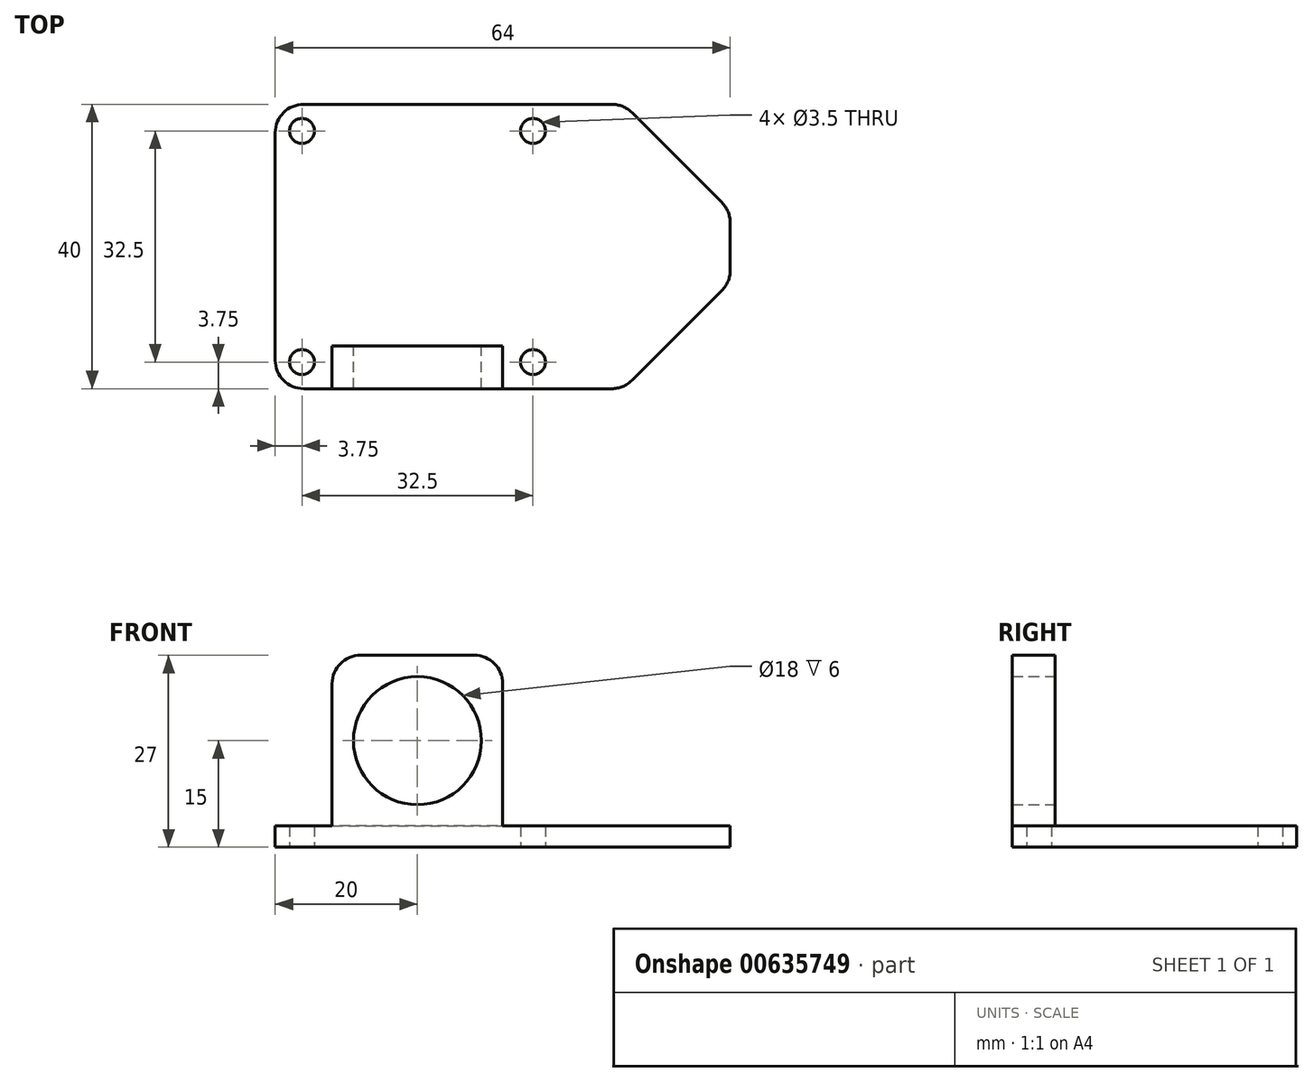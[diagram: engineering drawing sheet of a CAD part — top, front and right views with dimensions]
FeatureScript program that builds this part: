
annotation { "Feature Type Name" : "Feature", "Feature Type Description" : "" }
export const myFeature = defineFeature(function(context is Context, id is Id, definition is map)
    precondition{}
    {
        {
            var Q0;
            Q0=qCreatedBy(makeId("Top.planeOp"),FACE);
            var sketch = newSketch(context, id + "F0", { "sketchPlane" : qUnion([Q0])});
            skLineSegment(sketch, "E0.bottom", {"start": v(20, -20) * mm, "end": v(-20, -20) * mm});
            skLineSegment(sketch, "E0.top", {"start": v(20, 20) * mm, "end": v(-20, 20) * mm});
            skLineSegment(sketch, "E0.left", {"start": v(20, -20) * mm, "end": v(20, 20) * mm});
            skLineSegment(sketch, "E0.right", {"start": v(-20, -20) * mm, "end": v(-20, 20) * mm});
            skPoint(sketch, "E0.middle", {"position": v(0, 0) * mm});
            skCircle(sketch, "E1", {"center": v(-16.25, 16.25) * mm, "radius": 1.75 * mm});
            skCircle(sketch, "E2", {"center": v(16.25, 16.25) * mm, "radius": 1.75 * mm});
            skCircle(sketch, "E3", {"center": v(16.25, -16.25) * mm, "radius": 1.75 * mm});
            skCircle(sketch, "E4", {"center": v(-16.25, -16.25) * mm, "radius": 1.75 * mm});
            skSolve(sketch);
        }
        {
            var Q0;
            Q0=makeQuery(id+"F0.imprint","IMPRINT",FACE,{"disambiguationData":[TD([[makeQuery(id+"F0.imprint","IMPRINT",EDGE,{"derivedFrom":sQuery(id+"F0.wireOp",EDGE,"E0.bottom")}),-1.0]])]});
            extrude(context, id + "F1", {"entities" : qUnion([Q0]), "depth" : 3 * mm, "offsetDistance" : 25 * mm});
        }
        {
            var Q0;
            {var subQ0=sQuery(id+"F0.wireOp",EDGE,"E0.right");Q0=makeQuery(id+"F8QHIOm5U3Bt2tr_1.boolean.opBoolean","MERGE",FACE,{"derivedFrom":[makeQuery(id+"F1.opExtrude","CAP_FACE",FACE,{"disambiguationData":[OSD([sQuery(id+"F0.wireOp",EDGE,"E0.bottom"),sQuery(id+"F0.wireOp",EDGE,"E0.top"),sQuery(id+"F0.wireOp",EDGE,"E0.left"),subQ0,sQuery(id+"F0.wireOp",EDGE,"E1"),sQuery(id+"F0.wireOp",EDGE,"E2"),sQuery(id+"F0.wireOp",EDGE,"E3"),sQuery(id+"F0.wireOp",EDGE,"E4")])],"isStart":false}),makeQuery(id+"F8QHIOm5U3Bt2tr_1.opExtrude","SWEPT_FACE",FACE,{"disambiguationData":[OSD([subQ0]),TDD([makeQuery(id+"F1.opExtrude","CAP_EDGE",EDGE,{"disambiguationData":[OSD([subQ0])],"isStart":false})])]})]});}
            var sketch = newSketch(context, id + "F2", { "sketchPlane" : qUnion([Q0])});
            skLineSegment(sketch, "E5.bottom", {"start": v(-12, -20) * mm, "end": v(12, -20) * mm});
            skLineSegment(sketch, "E5.top", {"start": v(-12, -14) * mm, "end": v(12, -14) * mm});
            skLineSegment(sketch, "E5.left", {"start": v(-12, -20) * mm, "end": v(-12, -14) * mm});
            skLineSegment(sketch, "E5.right", {"start": v(12, -20) * mm, "end": v(12, -14) * mm});
            skSolve(sketch);
        }
        {
            var Q0;
            Q0 = qSketchRegion(id + "F2", true);
            extrude(context, id + "F3", {"entities" : qUnion([Q0]), "operationType" : NewBodyOperationType.ADD, "depth" : 24 * mm, "offsetDistance" : 25 * mm});
        }
        {
            var Q0;
            Q0=makeQuery(id+"F3.opExtrude","SWEPT_FACE",FACE,{"disambiguationData":[OSD([sQuery(id+"F2.wireOp",EDGE,"E5.top")])]});
            var sketch = newSketch(context, id + "F4", { "sketchPlane" : qUnion([Q0])});
            skCircle(sketch, "E6", {"center": v(0, 15) * mm, "radius": 9 * mm});
            skSolve(sketch);
        }
        {
            var Q0;
            Q0 = qSketchRegion(id + "F4", true);
            extrude(context, id + "F5", {"entities" : qUnion([Q0]), "operationType" : NewBodyOperationType.REMOVE, "oppositeDirection" : true, "depth" : 25 * mm, "offsetDistance" : 25 * mm});
        }
        {
            var Q0;
            Q0=makeQuery(id+"F1.opExtrude","SWEPT_FACE",FACE,{"disambiguationData":[OSD([sQuery(id+"F0.wireOp",EDGE,"E0.left")])]});
            extrude(context, id + "F6", {"entities" : qUnion([Q0]), "operationType" : NewBodyOperationType.ADD, "depth" : 24 * mm, "offsetDistance" : 25 * mm});
        }
        {
            var Q0;
            Q0=makeQuery(id+"F6.opExtrude","CAP_EDGE",EDGE,{"disambiguationData":[OSD([sQuery(id+"F0.wireOp",EDGE,"E0.top"),sQuery(id+"F0.wireOp",EDGE,"E0.left")])],"isStart":false});
            var Q1;
            Q1=makeQuery(id+"F6.opExtrude","CAP_EDGE",EDGE,{"disambiguationData":[OSD([sQuery(id+"F0.wireOp",EDGE,"E0.bottom"),sQuery(id+"F0.wireOp",EDGE,"E0.left")])],"isStart":false});
            chamfer(context, id + "F7", {"entities" : qUnion([Q0, Q1]), "width" : 15 * mm, "tangentPropagation" : true});
        }
        {
            var Q0;
            {var subQ0=sQuery(id+"F0.wireOp",EDGE,"E0.left");var subQ1=sQuery(id+"F0.wireOp",EDGE,"E0.top");Q0=makeQuery(id+"F7.opChamfer","BLEND_EDGE",EDGE,{"blendedFrom":[makeQuery(id+"F6.opExtrude","CAP_EDGE",EDGE,{"disambiguationData":[OSD([subQ1,subQ0])],"isStart":false}),makeQuery(id+"F6.boolean.opBoolean","MERGE",FACE,{"derivedFrom":[makeQuery(id+"F1.opExtrude","SWEPT_FACE",FACE,{"disambiguationData":[OSD([subQ1])]}),makeQuery(id+"F6.opExtrude","SWEPT_FACE",FACE,{"disambiguationData":[OSD([subQ1,subQ0])]})]})],"blendedInto":[makeQuery(id+"F6.boolean.opBoolean","MERGE",FACE,{"derivedFrom":[makeQuery(id+"F1.opExtrude","SWEPT_FACE",FACE,{"disambiguationData":[OSD([subQ1])]}),makeQuery(id+"F6.opExtrude","SWEPT_FACE",FACE,{"disambiguationData":[OSD([subQ1,subQ0])]})]})]});}
            var Q1;
            {var subQ0=sQuery(id+"F0.wireOp",EDGE,"E0.left");Q1=makeQuery(id+"F7.opChamfer","BLEND_EDGE",EDGE,{"blendedFrom":[makeQuery(id+"F6.opExtrude","CAP_EDGE",EDGE,{"disambiguationData":[OSD([sQuery(id+"F0.wireOp",EDGE,"E0.top"),subQ0])],"isStart":false}),makeQuery(id+"F6.opExtrude","CAP_FACE",FACE,{"disambiguationData":[OSD([subQ0])],"isStart":false})],"blendedInto":[makeQuery(id+"F6.opExtrude","CAP_FACE",FACE,{"disambiguationData":[OSD([subQ0])],"isStart":false})]});}
            var Q2;
            Q2=makeQuery(id+"F1.opExtrude","SWEPT_EDGE",EDGE,{"disambiguationData":[OSD([sQuery(id+"F0.wireOp",EDGE,"E0.top"),sQuery(id+"F0.wireOp",EDGE,"E0.right")])]});
            var Q3;
            Q3=makeQuery(id+"F1.opExtrude","SWEPT_EDGE",EDGE,{"disambiguationData":[OSD([sQuery(id+"F0.wireOp",EDGE,"E0.bottom"),sQuery(id+"F0.wireOp",EDGE,"E0.right")])]});
            var Q4;
            {var subQ0=sQuery(id+"F0.wireOp",EDGE,"E0.left");var subQ1=sQuery(id+"F0.wireOp",EDGE,"E0.bottom");Q4=makeQuery(id+"F7.opChamfer","BLEND_EDGE",EDGE,{"blendedFrom":[makeQuery(id+"F6.opExtrude","CAP_EDGE",EDGE,{"disambiguationData":[OSD([subQ1,subQ0])],"isStart":false}),makeQuery(id+"F6.boolean.opBoolean","MERGE",FACE,{"derivedFrom":[makeQuery(id+"F3.boolean.opBoolean","MERGE",FACE,{"derivedFrom":[makeQuery(id+"F1.opExtrude","SWEPT_FACE",FACE,{"disambiguationData":[OSD([subQ1])]}),makeQuery(id+"F3.opExtrude","SWEPT_FACE",FACE,{"disambiguationData":[OSD([sQuery(id+"F2.wireOp",EDGE,"E5.bottom")])]})]}),makeQuery(id+"F6.opExtrude","SWEPT_FACE",FACE,{"disambiguationData":[OSD([subQ1,subQ0])]})]})],"blendedInto":[makeQuery(id+"F6.boolean.opBoolean","MERGE",FACE,{"derivedFrom":[makeQuery(id+"F3.boolean.opBoolean","MERGE",FACE,{"derivedFrom":[makeQuery(id+"F1.opExtrude","SWEPT_FACE",FACE,{"disambiguationData":[OSD([subQ1])]}),makeQuery(id+"F3.opExtrude","SWEPT_FACE",FACE,{"disambiguationData":[OSD([sQuery(id+"F2.wireOp",EDGE,"E5.bottom")])]})]}),makeQuery(id+"F6.opExtrude","SWEPT_FACE",FACE,{"disambiguationData":[OSD([subQ1,subQ0])]})]})]});}
            var Q5;
            {var subQ0=sQuery(id+"F0.wireOp",EDGE,"E0.left");Q5=makeQuery(id+"F7.opChamfer","BLEND_EDGE",EDGE,{"blendedFrom":[makeQuery(id+"F6.opExtrude","CAP_EDGE",EDGE,{"disambiguationData":[OSD([sQuery(id+"F0.wireOp",EDGE,"E0.bottom"),subQ0])],"isStart":false}),makeQuery(id+"F6.opExtrude","CAP_FACE",FACE,{"disambiguationData":[OSD([subQ0])],"isStart":false})],"blendedInto":[makeQuery(id+"F6.opExtrude","CAP_FACE",FACE,{"disambiguationData":[OSD([subQ0])],"isStart":false})]});}
            var Q6;
            Q6=makeQuery(id+"F3.opExtrude","CAP_EDGE",EDGE,{"disambiguationData":[OSD([sQuery(id+"F2.wireOp",EDGE,"E5.left")])],"isStart":false});
            var Q7;
            Q7=makeQuery(id+"F3.opExtrude","CAP_EDGE",EDGE,{"disambiguationData":[OSD([sQuery(id+"F2.wireOp",EDGE,"E5.right")])],"isStart":false});
            fillet(context, id + "F8", {"entities" : qUnion([Q0, Q1, Q2, Q3, Q4, Q5, Q6, Q7]), "radius" : 4 * mm, "tangentPropagation" : true, "allowEdgeOverflow" : false});
        }
    });
